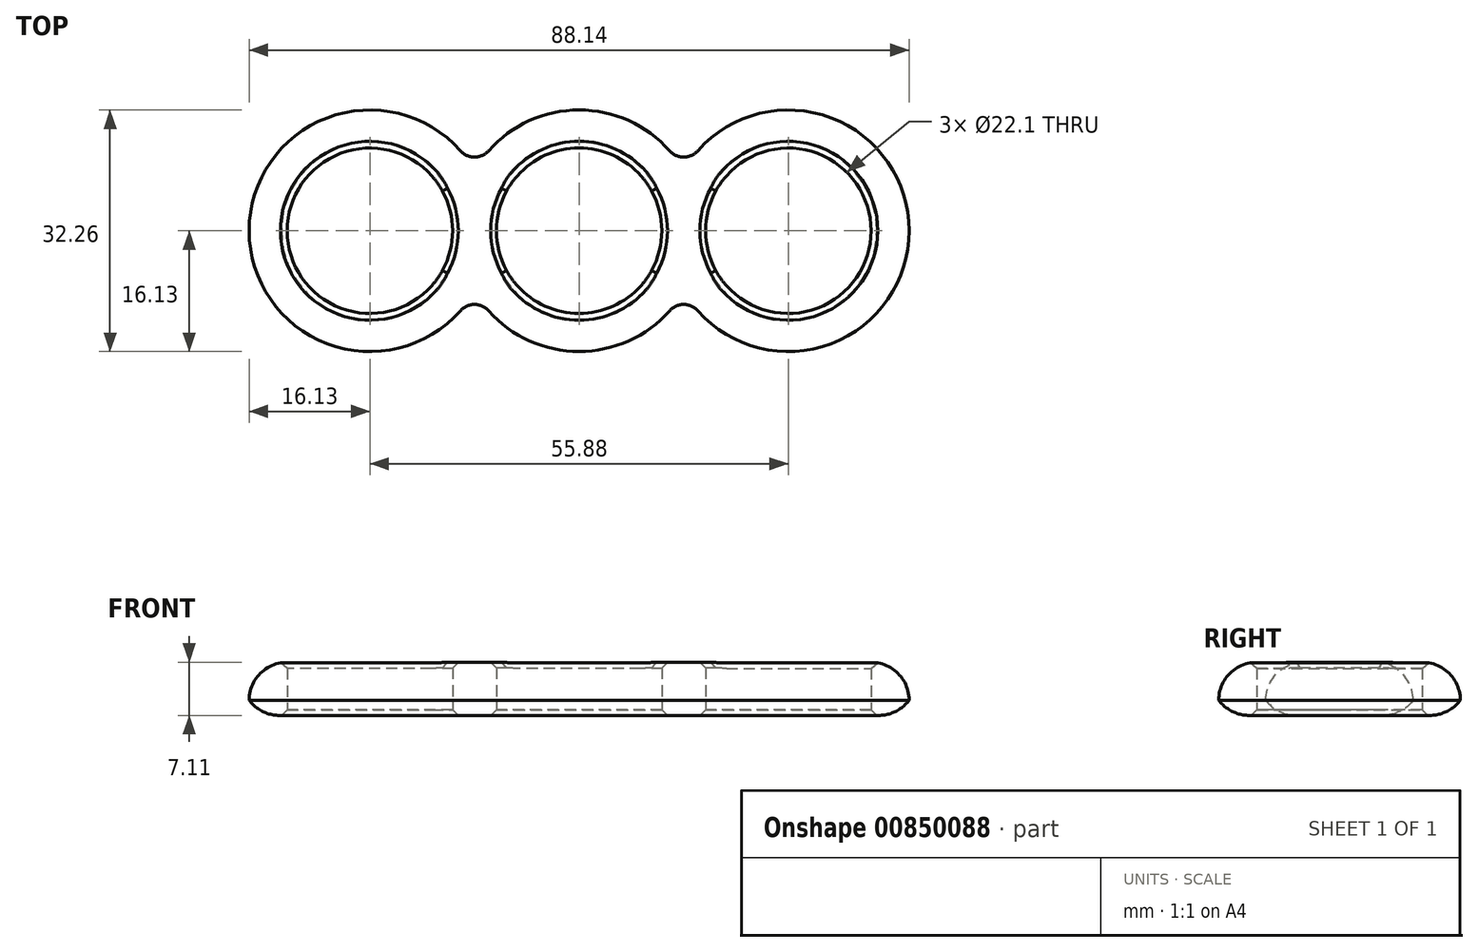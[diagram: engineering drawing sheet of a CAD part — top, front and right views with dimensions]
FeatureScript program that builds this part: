
annotation { "Feature Type Name" : "Feature", "Feature Type Description" : "" }
export const myFeature = defineFeature(function(context is Context, id is Id, definition is map)
    precondition{}
    {
        {
            var Q0;
            Q0=qCreatedBy(makeId("Top.planeOp"),FACE);
            var sketch = newSketch(context, id + "F0", { "sketchPlane" : qUnion([Q0])});
            skCircle(sketch, "E0", {"center": v(0, 0) * mm, "radius": 11.05 * mm});
            skCircle(sketch, "E1", {"center": v(27.94, 0) * mm, "radius": 11.05 * mm});
            skCircle(sketch, "E2.MirrorC", {"center": v(-27.94, 0) * mm, "radius": 11.05 * mm});
            skArc(sketch, "E3.0", {"start": v(-12.07, -10.7) * mm, "mid": v(0, -16.13) * mm, "end": v(12.07, -10.7) * mm});
            skArc(sketch, "E4.0", {"start": v(15.87, -10.7) * mm, "mid": v(44.07, 0) * mm, "end": v(15.87, 10.7) * mm});
            skArc(sketch, "E5.0", {"start": v(-15.87, -10.7) * mm, "mid": v(-44.07, 0) * mm, "end": v(-15.87, 10.7) * mm});
            skArc(sketch, "E6.trimOffspring", {"start": v(12.07, 10.7) * mm, "mid": v(0, 16.13) * mm, "end": v(-12.07, 10.7) * mm});
            skPoint(sketch, "E7.visualSharp", {"position": v(-13.97, 8.06) * mm});
            skArc(sketch, "E7.filletArc", {"start": v(-15.87, 10.7) * mm, "mid": v(-13.97, 9.84) * mm, "end": v(-12.07, 10.7) * mm});
            skPoint(sketch, "E8.visualSharp", {"position": v(13.97, 8.06) * mm});
            skArc(sketch, "E8.filletArc", {"start": v(12.07, 10.7) * mm, "mid": v(13.97, 9.84) * mm, "end": v(15.87, 10.7) * mm});
            skPoint(sketch, "E9.visualSharp", {"position": v(13.97, -8.06) * mm});
            skArc(sketch, "E9.filletArc", {"start": v(15.87, -10.7) * mm, "mid": v(13.97, -9.84) * mm, "end": v(12.07, -10.7) * mm});
            skPoint(sketch, "E10.visualSharp", {"position": v(-13.97, -8.06) * mm});
            skArc(sketch, "E10.filletArc", {"start": v(-12.07, -10.7) * mm, "mid": v(-13.97, -9.84) * mm, "end": v(-15.87, -10.7) * mm});
            skSolve(sketch);
        }
        {
            var Q0;
            Q0=makeQuery(id+"F0.imprint","IMPRINT",FACE,{"disambiguationData":[TD([[makeQuery(id+"F0.imprint","IMPRINT",EDGE,{"derivedFrom":sQuery(id+"F0.wireOp",EDGE,"E0")}),-1.0]])]});
            extrude(context, id + "F1", {"entities" : qUnion([Q0]), "depth" : 7.11 * mm, "offsetDistance" : 25.4 * mm});
        }
        {
            var Q0;
            Q0=makeQuery(id+"F1.opExtrude","CAP_EDGE",EDGE,{"disambiguationData":[OSD([sQuery(id+"F0.wireOp",EDGE,"E4.0")])],"isStart":false});
            fillet(context, id + "F2", {"entities" : qUnion([Q0]), "radius" : 5.08 * mm, "tangentPropagation" : true, "allowEdgeOverflow" : false});
        }
        {
            var Q0;
            Q0=makeQuery(id+"F1.opExtrude","CAP_EDGE",EDGE,{"disambiguationData":[OSD([sQuery(id+"F0.wireOp",EDGE,"E5.0")])],"isStart":true});
            fillet(context, id + "F3", {"entities" : qUnion([Q0]), "radius" : 5.08 * mm, "tangentPropagation" : true, "allowEdgeOverflow" : false});
        }
        {
            var Q0;
            Q0=makeQuery(id+"F1.opExtrude","SWEPT_FACE",FACE,{"disambiguationData":[OSD([sQuery(id+"F0.wireOp",EDGE,"E2.MirrorC")])]});
            var Q1;
            Q1=makeQuery(id+"F1.opExtrude","SWEPT_FACE",FACE,{"disambiguationData":[OSD([sQuery(id+"F0.wireOp",EDGE,"E0")])]});
            var Q2;
            Q2=makeQuery(id+"F1.opExtrude","SWEPT_FACE",FACE,{"disambiguationData":[OSD([sQuery(id+"F0.wireOp",EDGE,"E1")])]});
            chamfer(context, id + "F4", {"entities" : qUnion([Q0, Q1, Q2]), "width" : 0.76 * mm, "tangentPropagation" : true});
        }
    });
